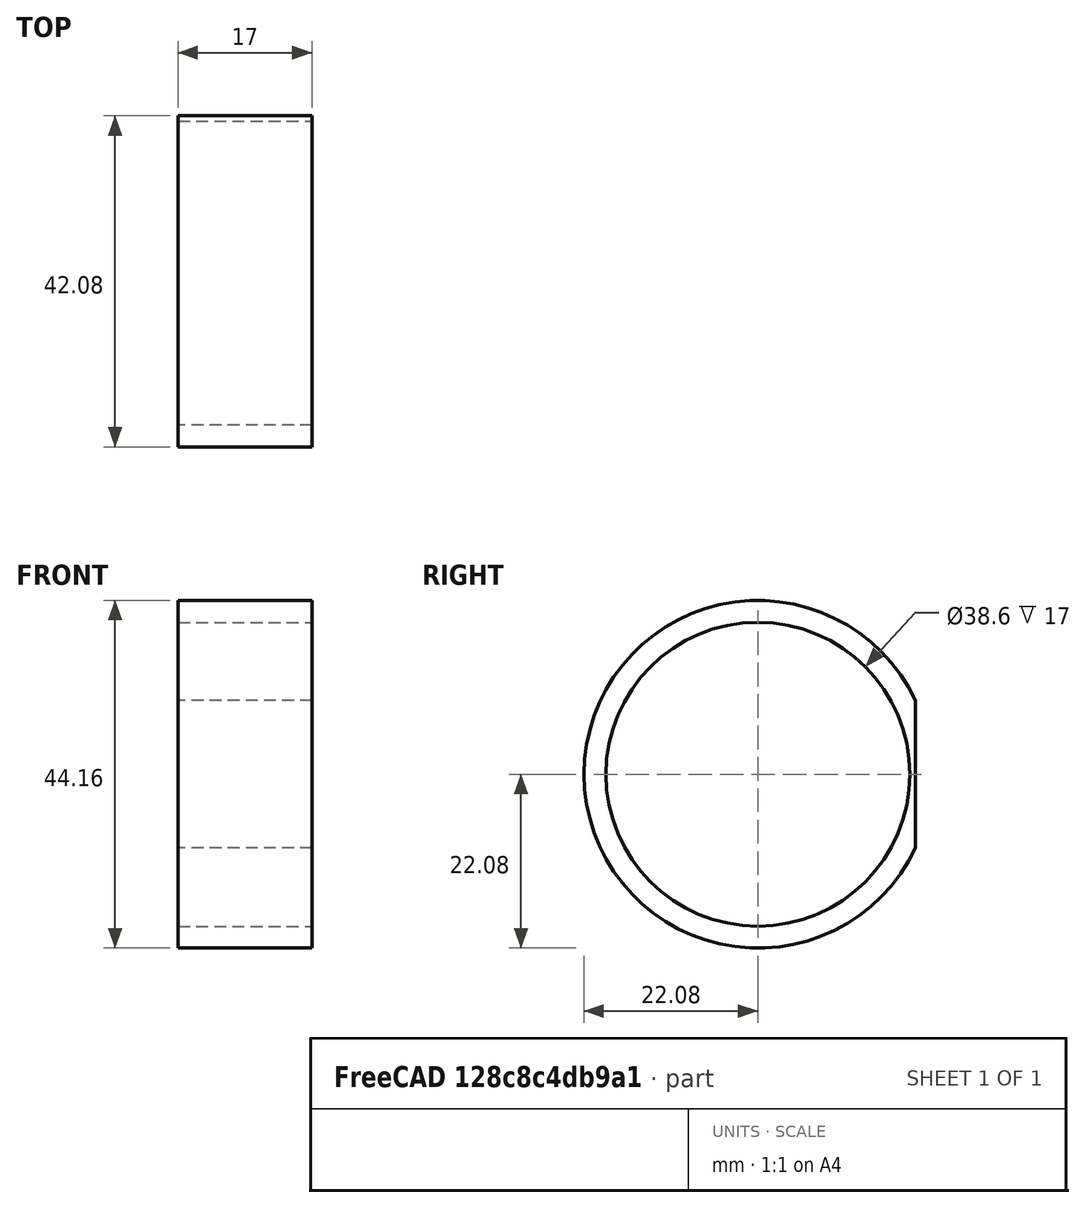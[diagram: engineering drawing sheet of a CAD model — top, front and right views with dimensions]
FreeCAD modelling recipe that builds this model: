
FCSTD DOCUMENT  (FreeCAD 0.18.4R)
Label: SoporteAngularMotor_CilindroMotor
License: All rights reserved
LicenseURL: http://en.wikipedia.org/wiki/All_rights_reserved
objects: Sketcher::SketchObject×1, PartDesign::Pad×1, PartDesign::Body×1, App::Part×1
note: 4 computed .brp shape members not serialized (recipe doc carries the construction recipe); baked Part::Feature solids carry a one-line shape summary decoded from their .brp

FEATURE [Sketcher::SketchObject] Sketch006  label="Sketch2_CilindroMotor"
  MapMode = 5
  Placement = pos=(7,-2e-15,2e-15) rot=(0.57735,-0.57735,-0.57735;2.0944rad)
  sketch-geometry (3):
    g0: Circle CenterX=0 CenterY=0 CenterZ=0 NormalX=0 NormalY=0 NormalZ=1 AngleXU=0 Radius=19.3
    g1: ArcOfCircle CenterX=0 CenterY=0 CenterZ=0 NormalX=0 NormalY=0 NormalZ=1 AngleXU=0 Radius=22.08 StartAngle=3.57913 EndAngle=8.98724
    g2: LineSegment StartX=-20 StartY=9.35555 StartZ=0 EndX=-20 EndY=-9.35555 EndZ=0
  constraints (9):
    c: Coincident(g0,g-1)
    c: Coincident(g1,g0)
    c: Radius(g0) = 19.3
    c: PointOnObject(g2,g1)
    c: Vertical(g2)
    c: DistanceX(g2,g0) = 20
    c: Radius(g1) = 22.08
    c: Coincident(g1,g2)
    c: Coincident(g1,g2)
FEATURE [PartDesign::Pad] Pad006  label="CilindroMotor_Extrusion2"
  Length = 17
  Length2 = 100
  Placement = pos=(7,-2e-15,2e-15) rot=(0.57735,-0.57735,-0.57735;2.0944rad)
  Profile = -> Sketch006
  Type = 0
FEATURE [PartDesign::Body] Body001  label="CilindroReduccion"
  Group = -> [Sketch006,Pad006]
  Origin = -> Origin002
  Tip = -> Pad006
FEATURE [App::Part] Part  label="SoporteAngularMotor_v2"
  Group = -> [Body001]
  Origin = -> Origin
